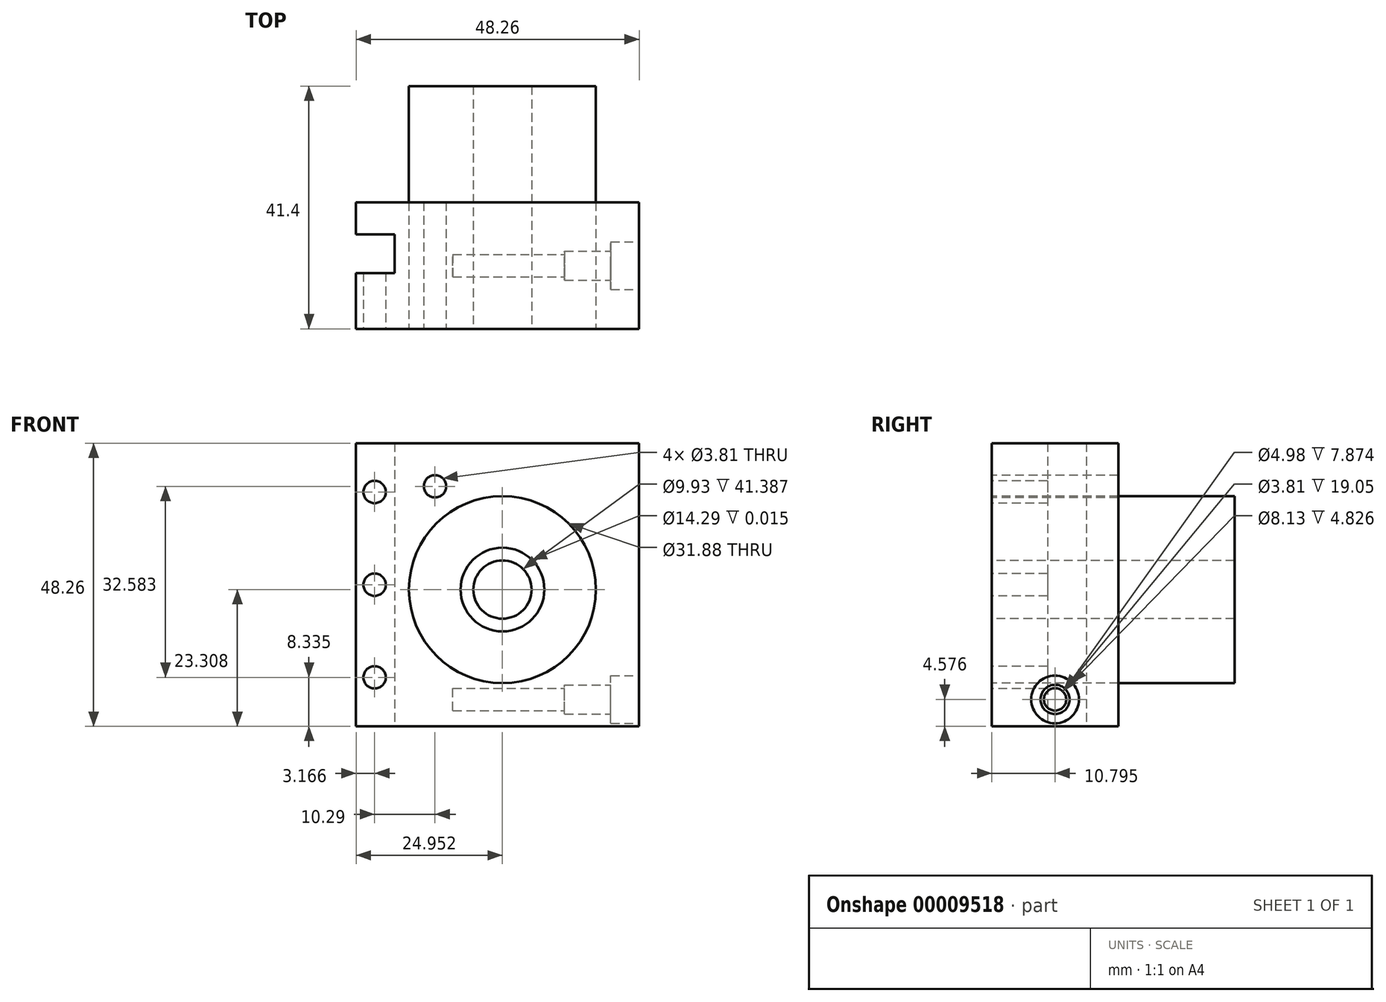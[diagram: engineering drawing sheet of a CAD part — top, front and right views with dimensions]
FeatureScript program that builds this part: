
annotation { "Feature Type Name" : "Feature", "Feature Type Description" : "" }
export const myFeature = defineFeature(function(context is Context, id is Id, definition is map)
    precondition{}
    {
        {
            var Q0;
            Q0=qCreatedBy(makeId("Front.planeOp"),FACE);
            var sketch = newSketch(context, id + "F0", { "sketchPlane" : qUnion([Q0])});
            skLineSegment(sketch, "E0.bottom", {"start": v(-180.25, 28.04) * mm, "end": v(-132, 28.04) * mm});
            skLineSegment(sketch, "E0.top", {"start": v(-180.25, -20.22) * mm, "end": v(-149.6, -20.22) * mm});
            skLineSegment(sketch, "E0.left", {"start": v(-180.25, 28.04) * mm, "end": v(-180.25, -20.22) * mm});
            skLineSegment(sketch, "E0.right", {"start": v(-132, 28.04) * mm, "end": v(-132, -20.22) * mm});
            skCircle(sketch, "E1", {"center": v(-155.3, 3.09) * mm, "radius": 15.94 * mm});
            skLineSegment(sketch, "E2", {"start": v(-155.3, 3.09) * mm, "end": v(-130.34, 3.09) * mm, "construction": true});
            skLineSegment(sketch, "E3", {"start": v(-155.3, 3.09) * mm, "end": v(-155.3, -21.87) * mm, "construction": true});
            skLineSegment(sketch, "E4", {"start": v(-173.65, -20.22) * mm, "end": v(-173.65, 28.04) * mm, "construction": true});
            skLineSegment(sketch, "E5", {"start": v(-177.08, 28.04) * mm, "end": v(-177.08, -20.22) * mm, "construction": true});
            skCircle(sketch, "E6", {"center": v(-177.08, 19.73) * mm, "radius": 1.9 * mm});
            skCircle(sketch, "E7", {"center": v(-177.08, 3.91) * mm, "radius": 1.9 * mm});
            skCircle(sketch, "E8", {"center": v(-177.08, -11.89) * mm, "radius": 1.9 * mm});
            skCircle(sketch, "E9", {"center": v(-166.8, 20.7) * mm, "radius": 1.9 * mm});
            skCircle(sketch, "E10", {"center": v(-155.3, 3.09) * mm, "radius": 4.97 * mm});
            skCircle(sketch, "E11", {"center": v(-155.3, 3.09) * mm, "radius": 7.14 * mm});
            skLineSegment(sketch, "E12.trimOffspring", {"start": v(-146.3, -20.22) * mm, "end": v(-132, -20.22) * mm});
            skCircle(sketch, "E13", {"center": v(-166.8, 20.7) * mm, "radius": 2.45 * mm});
            skLineSegment(sketch, "E14", {"start": v(-149.6, -20.22) * mm, "end": v(-146.3, -20.22) * mm});
            skSolve(sketch);
        }
        {
            var Q0;
            Q0=makeQuery(id+"F0.imprint","IMPRINT",FACE,{"disambiguationData":[TD([[makeQuery(id+"F0.imprint","IMPRINT",EDGE,{"derivedFrom":sQuery(id+"F0.wireOp",EDGE,"E0.bottom")}),-1.0]])]});
            var Q1;
            Q1=makeQuery(id+"F0.imprint","IMPRINT",FACE,{"disambiguationData":[TD([[makeQuery(id+"F0.imprint","IMPRINT",EDGE,{"derivedFrom":sQuery(id+"F0.wireOp",EDGE,"E9")}),1.0]])]});
            var Q2;
            Q2=makeQuery(id+"F0.imprint","IMPRINT",FACE,{"disambiguationData":[TD([[makeQuery(id+"F0.imprint","IMPRINT",EDGE,{"derivedFrom":sQuery(id+"F0.wireOp",EDGE,"E6")}),1.0]])]});
            var Q3;
            Q3=makeQuery(id+"F0.imprint","IMPRINT",FACE,{"disambiguationData":[TD([[makeQuery(id+"F0.imprint","IMPRINT",EDGE,{"derivedFrom":sQuery(id+"F0.wireOp",EDGE,"E7")}),1.0]])]});
            var Q4;
            Q4=makeQuery(id+"F0.imprint","IMPRINT",FACE,{"disambiguationData":[TD([[makeQuery(id+"F0.imprint","IMPRINT",EDGE,{"derivedFrom":sQuery(id+"F0.wireOp",EDGE,"E8")}),1.0]])]});
            var Q5;
            Q5=makeQuery(id+"F0.imprint","IMPRINT",FACE,{"disambiguationData":[TD([[makeQuery(id+"F0.imprint","IMPRINT",EDGE,{"derivedFrom":sQuery(id+"F0.wireOp",EDGE,"E9")}),-1.0]])]});
            var Q6;
            {var subQ1=sQuery(id+"F0.wireOp",EDGE,"2551a94f-3a1d-4b0e-8204-0523b05fb9c7");Q6=makeQuery(id+"F0.imprint","IMPRINT",FACE,{"disambiguationData":[TD([[makeQuery(id+"F0.imprint","IMPRINT",EDGE,{"derivedFrom":subQ1}),1.0]])]});}
            extrude(context, id + "F1", {"entities" : qUnion([Q0, Q1, Q2, Q3, Q4, Q5, Q6]), "oppositeDirection" : true, "depth" : 21.59 * mm});
        }
        {
            var Q0;
            Q0=makeQuery(id+"F0.imprint","IMPRINT",FACE,{"disambiguationData":[TD([[makeQuery(id+"F0.imprint","IMPRINT",EDGE,{"derivedFrom":sQuery(id+"F0.wireOp",EDGE,"E11")}),-1.0]])]});
            var Q1;
            Q1=makeQuery(id+"F0.imprint","IMPRINT",FACE,{"disambiguationData":[TD([[makeQuery(id+"F0.imprint","IMPRINT",EDGE,{"derivedFrom":sQuery(id+"F0.wireOp",EDGE,"E10")}),-1.0]])]});
            var Q2;
            Q2=makeQuery(id+"F0.imprint","IMPRINT",FACE,{"disambiguationData":[TD([[makeQuery(id+"F0.imprint","IMPRINT",EDGE,{"derivedFrom":sQuery(id+"F0.wireOp",EDGE,"E10")}),1.0]])]});
            extrude(context, id + "F2", {"entities" : qUnion([Q0, Q1, Q2]), "oppositeDirection" : true, "depth" : 41.4 * mm});
        }
        {
            var Q0;
            Q0=makeQuery(id+"F0.imprint","IMPRINT",FACE,{"disambiguationData":[TD([[makeQuery(id+"F0.imprint","IMPRINT",EDGE,{"derivedFrom":sQuery(id+"F0.wireOp",EDGE,"E10")}),1.0]])]});
            extrude(context, id + "F3", {"entities" : qUnion([Q0]), "operationType" : NewBodyOperationType.REMOVE, "endBound" : BoundingType.UP_TO_NEXT, "oppositeDirection" : true, "depth" : 25.4 * mm});
        }
        {
            var Q0;
            Q0=makeQuery(id+"F0.imprint","IMPRINT",FACE,{"disambiguationData":[TD([[makeQuery(id+"F0.imprint","IMPRINT",EDGE,{"derivedFrom":sQuery(id+"F0.wireOp",EDGE,"E10")}),-1.0]])]});
            extrude(context, id + "F4", {"entities" : qUnion([Q0]), "operationType" : NewBodyOperationType.REMOVE, "oppositeDirection" : true, "depth" : 3 / 203.2 * mm});
        }
        {
            var Q0;
            Q0=makeQuery(id+"F1.opExtrude","SWEPT_FACE",FACE,{"disambiguationData":[OSD([sQuery(id+"F0.wireOp",EDGE,"E0.top")])]});
            var sketch = newSketch(context, id + "F5", { "sketchPlane" : qUnion([Q0])});
            skLineSegment(sketch, "E15.0", {"start": v(-180.25, -21.59) * mm, "end": v(-180.25, -16.13) * mm, "construction": true});
            skLineSegment(sketch, "E16.0", {"start": v(-180.25, 0) * mm, "end": v(-149.6, 0) * mm, "construction": true});
            skLineSegment(sketch, "E17.0", {"start": v(-180.25, -21.59) * mm, "end": v(-180.25, -21.59) * mm});
            skLineSegment(sketch, "E18.bottom", {"start": v(-180.25, -9.53) * mm, "end": v(-173.65, -9.53) * mm});
            skLineSegment(sketch, "E18.top", {"start": v(-180.25, -16.13) * mm, "end": v(-173.65, -16.13) * mm});
            skLineSegment(sketch, "E18.left", {"start": v(-180.25, -9.53) * mm, "end": v(-180.25, -16.13) * mm});
            skLineSegment(sketch, "E18.right", {"start": v(-173.65, -9.53) * mm, "end": v(-173.65, -16.13) * mm});
            skLineSegment(sketch, "E19", {"start": v(-180.25, -9.53) * mm, "end": v(-180.25, 0) * mm, "construction": true});
            skLineSegment(sketch, "E20", {"start": v(-180.25, -16.13) * mm, "end": v(-180.25, -9.53) * mm, "construction": true});
            skLineSegment(sketch, "E21.0", {"start": v(-132, 0) * mm, "end": v(-132, 0) * mm});
            skLineSegment(sketch, "E22.0", {"start": v(-132, -21.59) * mm, "end": v(-132, -21.59) * mm});
            skLineSegment(sketch, "E23", {"start": v(-136.82, 0) * mm, "end": v(-136.82, -21.59) * mm, "construction": true});
            skLineSegment(sketch, "E24", {"start": v(-163.74, 0) * mm, "end": v(-163.74, -21.59) * mm, "construction": true});
            skLineSegment(sketch, "E25", {"start": v(-162.22, 0) * mm, "end": v(-162.22, -21.59) * mm, "construction": true});
            skSolve(sketch);
        }
        {
            var Q0;
            Q0=makeQuery(id+"F5.imprint","IMPRINT",FACE,{"disambiguationData":[TD([[makeQuery(id+"F5.imprint","IMPRINT",EDGE,{"derivedFrom":sQuery(id+"F5.wireOp",EDGE,"E18.bottom")}),-1.0]])]});
            extrude(context, id + "F6", {"entities" : qUnion([Q0]), "operationType" : NewBodyOperationType.REMOVE, "endBound" : BoundingType.UP_TO_NEXT, "oppositeDirection" : true, "depth" : 25.4 * mm});
        }
        {
            var Q0;
            Q0=makeQuery(id+"F0.imprint","IMPRINT",FACE,{"disambiguationData":[TD([[makeQuery(id+"F0.imprint","IMPRINT",EDGE,{"derivedFrom":sQuery(id+"F0.wireOp",EDGE,"E9")}),1.0]])]});
            extrude(context, id + "F7", {"entities" : qUnion([Q0]), "operationType" : NewBodyOperationType.REMOVE, "endBound" : BoundingType.UP_TO_NEXT, "oppositeDirection" : true, "depth" : 25.4 * mm});
        }
        {
            var Q0;
            Q0=makeQuery(id+"F0.imprint","IMPRINT",FACE,{"disambiguationData":[TD([[makeQuery(id+"F0.imprint","IMPRINT",EDGE,{"derivedFrom":sQuery(id+"F0.wireOp",EDGE,"E6")}),1.0]])]});
            var Q1;
            Q1=makeQuery(id+"F0.imprint","IMPRINT",FACE,{"disambiguationData":[TD([[makeQuery(id+"F0.imprint","IMPRINT",EDGE,{"derivedFrom":sQuery(id+"F0.wireOp",EDGE,"E7")}),1.0]])]});
            var Q2;
            Q2=makeQuery(id+"F0.imprint","IMPRINT",FACE,{"disambiguationData":[TD([[makeQuery(id+"F0.imprint","IMPRINT",EDGE,{"derivedFrom":sQuery(id+"F0.wireOp",EDGE,"E8")}),1.0]])]});
            extrude(context, id + "F8", {"entities" : qUnion([Q0, Q1, Q2]), "operationType" : NewBodyOperationType.REMOVE, "endBound" : BoundingType.UP_TO_NEXT, "oppositeDirection" : true, "depth" : 25.4 * mm});
        }
        {
            var Q0;
            Q0=makeQuery(id+"F1.opExtrude","SWEPT_FACE",FACE,{"disambiguationData":[OSD([sQuery(id+"F0.wireOp",EDGE,"E0.right")])]});
            var sketch = newSketch(context, id + "F9", { "sketchPlane" : qUnion([Q0])});
            skLineSegment(sketch, "E26", {"start": v(12.7, -30.22) * mm, "end": v(12.7, 42.02) * mm, "construction": true});
            skLineSegment(sketch, "E27", {"start": v(0, -15.64) * mm, "end": v(21.59, -15.64) * mm, "construction": true});
            skCircle(sketch, "E28", {"center": v(10.8, -15.64) * mm, "radius": 4.06 * mm});
            skCircle(sketch, "E29", {"center": v(10.8, -15.64) * mm, "radius": 1.9 * mm});
            skCircle(sketch, "E30", {"center": v(10.8, -15.64) * mm, "radius": 2.49 * mm});
            skSolve(sketch);
        }
        {
            var Q0;
            Q0=makeQuery(id+"F9.imprint","IMPRINT",FACE,{"disambiguationData":[TD([[makeQuery(id+"F9.imprint","IMPRINT",EDGE,{"derivedFrom":sQuery(id+"F9.wireOp",EDGE,"E29")}),1.0]])]});
            extrude(context, id + "F10", {"entities" : qUnion([Q0]), "operationType" : NewBodyOperationType.REMOVE, "oppositeDirection" : true, "depth" : 31.75 * mm});
        }
        {
            var Q0;
            Q0=makeQuery(id+"F9.imprint","IMPRINT",FACE,{"disambiguationData":[TD([[makeQuery(id+"F9.imprint","IMPRINT",EDGE,{"derivedFrom":sQuery(id+"F9.wireOp",EDGE,"E29")}),-1.0]])]});
            extrude(context, id + "F11", {"entities" : qUnion([Q0]), "operationType" : NewBodyOperationType.REMOVE, "oppositeDirection" : true, "depth" : 12.7 * mm});
        }
        {
            var Q0;
            Q0=makeQuery(id+"F9.imprint","IMPRINT",FACE,{"disambiguationData":[TD([[makeQuery(id+"F9.imprint","IMPRINT",EDGE,{"derivedFrom":sQuery(id+"F9.wireOp",EDGE,"E28")}),1.0]])]});
            extrude(context, id + "F12", {"entities" : qUnion([Q0]), "operationType" : NewBodyOperationType.REMOVE, "oppositeDirection" : true, "depth" : 4.83 * mm});
        }
    });
